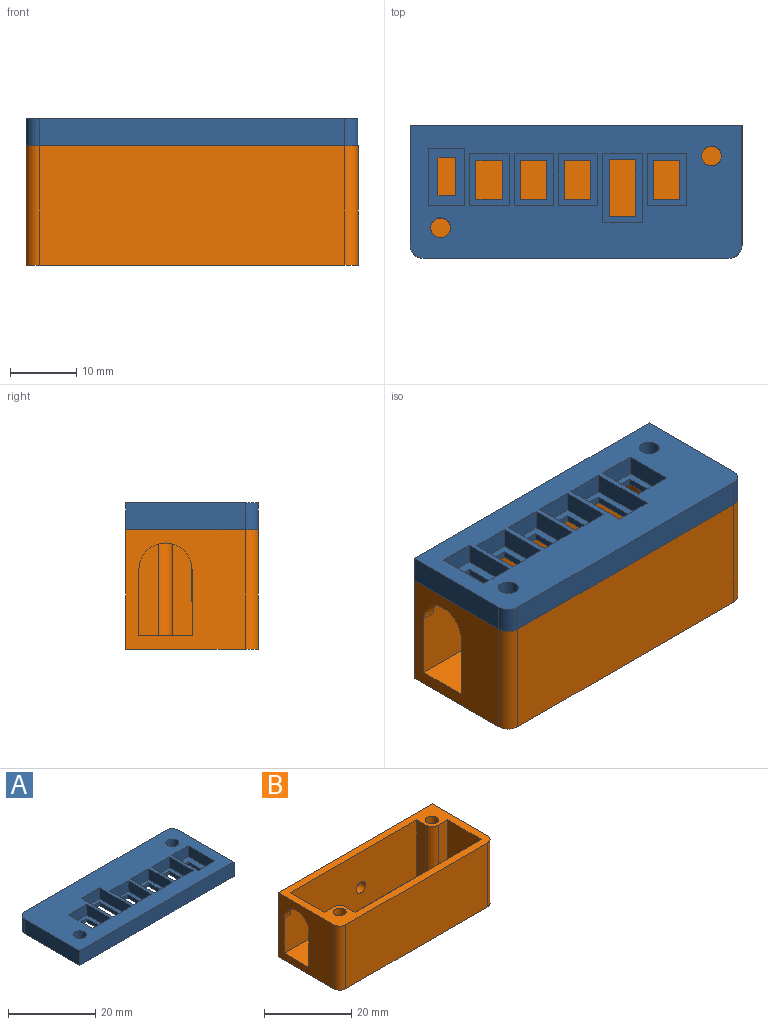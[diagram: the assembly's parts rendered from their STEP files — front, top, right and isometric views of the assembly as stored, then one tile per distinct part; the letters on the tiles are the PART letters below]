
ASSEMBLY  parts=2 mates=1
PART A: 64 faces, bbox 50x20x4.1 mm
  f0: cylinder r=2mm len=4.06mm, axis (0,0,-1), area 12.8mm2, adj f1,f24,f32,f33
  f1: plane 18x4.06mm, normal (-1,0,0), area 73.1mm2, adj f0,f2,f32,f33
  f2: plane 50x4.06mm, normal (0,-1,0), area 203mm2, adj f1,f3,f32,f33
  f3: plane 18x4.06mm, normal (1,0,0), area 73.1mm2, adj f2,f4,f32,f33
  f4: cylinder r=2mm len=4.06mm, axis (0,0,-1), area 12.8mm2, adj f3,f24,f32,f33
  f5: plane 7.72x3.06mm, normal (1,0,0), area 23.6mm2, adj f6,f25,f32,f38
  f6: plane 5.94x3.06mm, normal (0,-1,0), area 18.2mm2, adj f5,f7,f32,f38
  f7: plane 7.72x3.06mm, normal (-1,0,0), area 23.6mm2, adj f6,f25,f32,f38
  f8: plane 10.3x3.06mm, normal (1,0,0), area 31.5mm2, adj f9,f26,f32,f43
  f9: plane 5.94x3.06mm, normal (0,-1,0), area 18.2mm2, adj f8,f10,f32,f43
  f10: plane 10.3x3.06mm, normal (-1,0,0), area 31.5mm2, adj f9,f26,f32,f43
  f11: plane 7.72x3.06mm, normal (1,0,0), area 23.6mm2, adj f12,f27,f32,f48
  f12: plane 5.94x3.06mm, normal (0,-1,0), area 18.2mm2, adj f11,f13,f32,f48
  f13: plane 7.72x3.06mm, normal (-1,0,0), area 23.6mm2, adj f12,f27,f32,f48
  f14: plane 7.72x3.06mm, normal (1,0,0), area 23.6mm2, adj f15,f28,f32,f53
  f15: plane 5.94x3.06mm, normal (0,-1,0), area 18.2mm2, adj f14,f16,f32,f53
  f16: plane 7.72x3.06mm, normal (-1,0,0), area 23.6mm2, adj f15,f28,f32,f53
  f17: plane 7.72x3.06mm, normal (1,0,0), area 23.6mm2, adj f18,f29,f32,f58
  f18: plane 5.94x3.06mm, normal (0,-1,0), area 18.2mm2, adj f17,f19,f32,f58
  f19: plane 7.72x3.06mm, normal (-1,0,0), area 23.6mm2, adj f18,f29,f32,f58
  f20: plane 8.6x3.06mm, normal (1,0,0), area 26.3mm2, adj f21,f30,f32,f63
  f21: plane 5.45x3.06mm, normal (0,-1,0), area 16.7mm2, adj f20,f22,f32,f63
  f22: plane 8.6x3.06mm, normal (-1,0,0), area 26.3mm2, adj f21,f30,f32,f63
  f23: cylinder r=1.5mm len=4.06mm, axis (0,0,-1), area 38.3mm2, adj f32,f33
  f24: plane 46x4.06mm, normal (0,1,0), area 186.8mm2, adj f0,f4,f32,f33
  f25: plane 5.94x3.06mm, normal (0,1,0), area 18.2mm2, adj f5,f7,f32,f38
  f26: plane 5.94x3.06mm, normal (0,1,0), area 18.2mm2, adj f8,f10,f32,f43
  f27: plane 5.94x3.06mm, normal (0,1,0), area 18.2mm2, adj f11,f13,f32,f48
  f28: plane 5.94x3.06mm, normal (0,1,0), area 18.2mm2, adj f14,f16,f32,f53
  f29: plane 5.94x3.06mm, normal (0,1,0), area 18.2mm2, adj f17,f19,f32,f58
  f30: plane 5.45x3.06mm, normal (0,1,0), area 16.7mm2, adj f20,f22,f32,f63
  f31: cylinder r=1.5mm len=4.06mm, axis (0,0,-1), area 38.3mm2, adj f32,f33
  f32: plane 50x20mm, normal (0,0,1), area 692.7mm2, adj f0,f1,f2,f3,f4,f5,f6,f7
  f33: plane 50x20mm, normal (0,0,-1), area 842.9mm2, adj f0,f1,f2,f3,f4,f23,f24,f31
  f34: plane 5.84x1mm, normal (1,0,0), area 5.8mm2, adj f33,f35,f37,f38
  f35: plane 3.94x1mm, normal (0,-1,0), area 3.9mm2, adj f33,f34,f36,f38
  f36: plane 5.84x1mm, normal (-1,0,0), area 5.8mm2, adj f33,f35,f37,f38
  f37: plane 3.94x1mm, normal (0,1,0), area 3.9mm2, adj f33,f34,f36,f38
  f38: plane 7.72x5.94mm, normal (0,0,1), area 22.8mm2, adj f5,f6,f7,f25,f34,f35,f36,f37
  f39: plane 8.52x1mm, normal (1,0,0), area 8.5mm2, adj f33,f40,f42,f43
  f40: plane 3.94x1mm, normal (0,-1,0), area 3.9mm2, adj f33,f39,f41,f43
  f41: plane 8.52x1mm, normal (-1,0,0), area 8.5mm2, adj f33,f40,f42,f43
  f42: plane 3.94x1mm, normal (0,1,0), area 3.9mm2, adj f33,f39,f41,f43
  f43: plane 10.3x5.94mm, normal (0,0,1), area 27.6mm2, adj f8,f9,f10,f26,f39,f40,f41,f42
  f44: plane 5.84x1mm, normal (1,0,0), area 5.8mm2, adj f33,f45,f47,f48
  f45: plane 3.94x1mm, normal (0,-1,0), area 3.9mm2, adj f33,f44,f46,f48
  f46: plane 5.84x1mm, normal (-1,0,0), area 5.8mm2, adj f33,f45,f47,f48
  f47: plane 3.94x1mm, normal (0,1,0), area 3.9mm2, adj f33,f44,f46,f48
  f48: plane 7.72x5.94mm, normal (0,0,1), area 22.8mm2, adj f11,f12,f13,f27,f44,f45,f46,f47
  f49: plane 5.84x1mm, normal (1,0,0), area 5.8mm2, adj f33,f50,f52,f53
  f50: plane 3.94x1mm, normal (0,-1,0), area 3.9mm2, adj f33,f49,f51,f53
  f51: plane 5.84x1mm, normal (-1,0,0), area 5.8mm2, adj f33,f50,f52,f53
  f52: plane 3.94x1mm, normal (0,1,0), area 3.9mm2, adj f33,f49,f51,f53
  f53: plane 7.72x5.94mm, normal (0,0,1), area 22.8mm2, adj f14,f15,f16,f28,f49,f50,f51,f52
  f54: plane 5.84x1mm, normal (1,0,0), area 5.8mm2, adj f33,f55,f57,f58
  f55: plane 3.94x1mm, normal (0,-1,0), area 3.9mm2, adj f33,f54,f56,f58
  f56: plane 5.84x1mm, normal (-1,0,0), area 5.8mm2, adj f33,f55,f57,f58
  f57: plane 3.94x1mm, normal (0,1,0), area 3.9mm2, adj f33,f54,f56,f58
  f58: plane 7.72x5.94mm, normal (0,0,1), area 22.8mm2, adj f17,f18,f19,f29,f54,f55,f56,f57
  f59: plane 5.8x1mm, normal (-1,0,0), area 5.8mm2, adj f33,f60,f62,f63
  f60: plane 2.7x1mm, normal (0,1,0), area 2.7mm2, adj f33,f59,f61,f63
  f61: plane 5.8x1mm, normal (1,0,0), area 5.8mm2, adj f33,f60,f62,f63
  f62: plane 2.7x1mm, normal (0,-1,0), area 2.7mm2, adj f33,f59,f61,f63
  f63: plane 8.6x5.45mm, normal (0,0,1), area 31.2mm2, adj f20,f21,f22,f30,f59,f60,f61,f62
PART B: 26 faces, bbox 50x20x18 mm
  f0: plane 16x11mm, normal (-1,0,0), area 176mm2, adj f3,f10,f12,f20
  f1: plane 16x11mm, normal (1,0,0), area 70.9mm2, adj f4,f10,f12,f13,f14,f16
  f2: plane 18x18mm, normal (-1,0,0), area 218.9mm2, adj f4,f6,f7,f10,f11,f12,f13,f14
  f3: plane 41x16mm, normal (0,1,0), area 656mm2, adj f0,f10,f12,f17
  f4: plane 43x16mm, normal (0,-1,0), area 668.9mm2, adj f1,f2,f10,f12,f13,f15,f21
  f5: plane 18x18mm, normal (1,0,0), area 324mm2, adj f6,f9,f10,f11
  f6: plane 50x18mm, normal (0,1,0), area 892.9mm2, adj f2,f5,f10,f11,f15
  f7: cylinder r=2mm len=18mm, axis (0,0,-1), area 56.5mm2, adj f2,f8,f10,f11
  f8: plane 46x18mm, normal (0,-1,0), area 828mm2, adj f7,f9,f10,f11
  f9: cylinder r=2mm len=18mm, axis (0,0,-1), area 56.5mm2, adj f5,f8,f10,f11
  f10: plane 50x20mm, normal (0,0,1), area 296.4mm2, adj f0,f1,f2,f3,f4,f5,f6,f7
  f11: plane 50x20mm, normal (0,0,-1), area 998.3mm2, adj f2,f5,f6,f7,f8,f9
  f12: plane 48x16mm, normal (0,0,1), area 703.7mm2, adj f0,f1,f2,f3,f4,f14,f16,f17
  f13: cylinder r=4mm len=8mm, axis (-1,0,0), area 25.1mm2, adj f1,f2,f4,f14
  f14: plane 10x2mm, normal (0,1,0), area 20mm2, adj f1,f2,f12,f13
  f15: cylinder r=1.5mm len=3mm, axis (0,1,0), area 18.8mm2, adj f4,f6
  f16: plane 16x3mm, normal (0,1,0), area 48mm2, adj f1,f10,f12,f24
  f17: plane 16x3mm, normal (1,0,0), area 48mm2, adj f3,f10,f12,f24
  f18: cylinder r=1.5mm len=16mm, axis (0,0,-1), area 150.8mm2, adj f10,f19
  f19: plane 3x3mm, normal (0,0,1), area 7.1mm2, adj f18
  f20: plane 16x3mm, normal (0,-1,0), area 48mm2, adj f0,f10,f12,f25
  f21: plane 16x3mm, normal (-1,0,0), area 48mm2, adj f4,f10,f12,f25
  f22: cylinder r=1.5mm len=16mm, axis (0,0,-1), area 150.8mm2, adj f10,f23
  f23: plane 3x3mm, normal (0,0,1), area 7.1mm2, adj f22
  f24: cylinder r=2mm len=16mm, axis (0,0,1), area 50.3mm2, adj f10,f12,f16,f17
  f25: cylinder r=2mm len=16mm, axis (0,0,1), area 50.3mm2, adj f10,f12,f20,f21
PLACE A rot(axis=(0,0,-1),180deg) t=(-8.32,-0.73,8.88)mm
PLACE B t=(-8.32,-0.73,-9.12)mm
MATE fastened A.f23 <-> B.f18  axis (0,0,-1) through (-28.72,-6.13,8.88)mm
